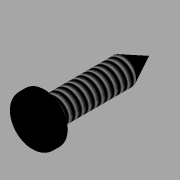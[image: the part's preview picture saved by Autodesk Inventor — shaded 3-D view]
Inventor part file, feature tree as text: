
AUTODESK INVENTOR PART (.ipt)
format: ipt  version: 2019 (Build 230136000, 136)  size: 126,464 bytes
history: native  units: mm
features: extrude x3, sketch x3, fillet x2, chamfer x1, thread x1
ambient origin geometry x8: Origin, YZ Plane, XZ Plane, XY Plane, X Axis, Y Axis, Z Axis, Center Point
bodies: Solid1 (feature_tree)
feature tree (10):
  extrude  "Extrusion1"  Depth=4.0mm TaperAngle=0.0deg
  extrude  "Extrusion2"  Depth=0.55mm TaperAngle=0.0deg
  chamfer  "Chamfer1"  Distance=0.5mm Angle=45.0deg
  fillet  "Fillet1"  Radius=0.2mm
  fillet  "Fillet2"  Radius=0.1mm
  extrude  "Extrusion3"  Depth=0.25mm
  thread  "Thread1"  [1 undecoded]
  sketch  "Sketch1"  dims[d0=1.0mm d1=4.0mm d2=0.0mm]
  sketch  "Sketch2"  dims[d3=1.85mm d4=0.55mm d5=0.0mm d6=0.5mm d7=1.0mm d8=45.0deg d9=0.2mm d10=0.1mm]
  sketch  "Sketch3"  dims[d11=1.15mm d12=0.25mm d13=0.25mm d14=1.15mm d15=0.25mm d16=0.0mm d17=10.0mm d18=0.0mm]
note: 1 required parameter value undecoded (feature->parameter linkage not recoverable at this tier; creation-order binding heuristic only, values carry confidence <= 0.55)
